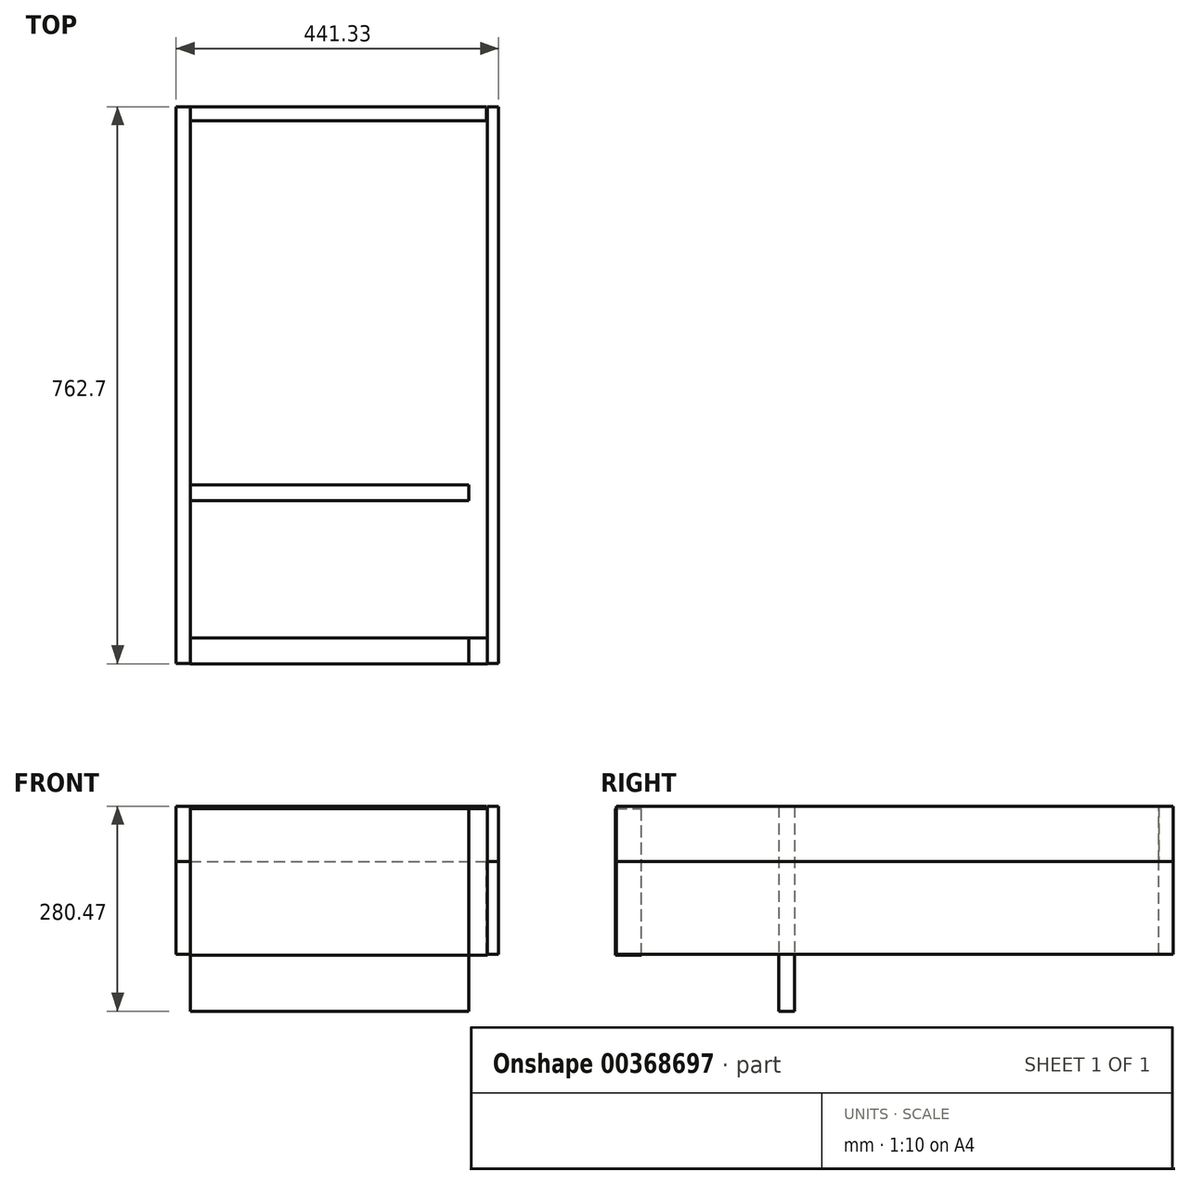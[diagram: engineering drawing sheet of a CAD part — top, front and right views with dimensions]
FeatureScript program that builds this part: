
annotation { "Feature Type Name" : "Feature", "Feature Type Description" : "" }
export const myFeature = defineFeature(function(context is Context, id is Id, definition is map)
    precondition{}
    {
        {
            var Q0;
            Q0=qCreatedBy(makeId("Front.planeOp"),FACE);
            var sketch = newSketch(context, id + "F0", { "sketchPlane" : qUnion([Q0])});
            skLineSegment(sketch, "E0.bottom", {"start": v(-75.87, 75.19) * mm, "end": v(75.87, 75.19) * mm});
            skLineSegment(sketch, "E0.top", {"start": v(-75.87, 0) * mm, "end": v(75.87, 0) * mm});
            skLineSegment(sketch, "E0.left", {"start": v(-75.87, 75.19) * mm, "end": v(-75.87, 0) * mm});
            skLineSegment(sketch, "E0.right", {"start": v(75.87, 75.19) * mm, "end": v(75.87, 0) * mm});
            skSolve(sketch);
        }
        {
            var Q0;
            Q0=makeQuery(id+"F0.imprint","IMPRINT",FACE,{"disambiguationData":[TD([[makeQuery(id+"F0.imprint","IMPRINT",EDGE,{"derivedFrom":sQuery(id+"F0.wireOp",EDGE,"E0.bottom")}),-1.0]])]});
            extrude(context, id + "F1", {"entities" : qUnion([Q0]), "depth" : 19.05 * mm});
        }
        {
            var Q0;
            Q0=qCreatedBy(makeId("Front.planeOp"),FACE);
            var sketch = newSketch(context, id + "F2", { "sketchPlane" : qUnion([Q0])});
            skLineSegment(sketch, "E1.bottom", {"start": v(-75.82, 75.3) * mm, "end": v(-94.93, 75.3) * mm});
            skLineSegment(sketch, "E1.top", {"start": v(-75.82, 3.74) * mm, "end": v(-94.93, 3.74) * mm});
            skLineSegment(sketch, "E1.left", {"start": v(-75.82, 75.3) * mm, "end": v(-75.82, 3.74) * mm});
            skLineSegment(sketch, "E1.right", {"start": v(-94.93, 75.3) * mm, "end": v(-94.93, 3.74) * mm});
            skSolve(sketch);
        }
        {
            var Q0;
            Q0=makeQuery(id+"F2.imprint","IMPRINT",FACE,{"disambiguationData":[TD([[makeQuery(id+"F2.imprint","IMPRINT",EDGE,{"derivedFrom":sQuery(id+"F2.wireOp",EDGE,"E1.bottom")}),1.0]])]});
            extrude(context, id + "F3", {"entities" : qUnion([Q0]), "operationType" : NewBodyOperationType.ADD, "depth" : 762 * mm});
        }
        {
            var Q0;
            Q0=makeQuery(id+"F3.opExtrude","SWEPT_FACE",FACE,{"disambiguationData":[OSD([sQuery(id+"F2.wireOp",EDGE,"E1.top")])]});
            extrude(context, id + "F4", {"entities" : qUnion([Q0]), "operationType" : NewBodyOperationType.ADD, "depth" : 3.8 * mm});
        }
        {
            var Q0;
            Q0=makeQuery(id+"F1.opExtrude","SWEPT_FACE",FACE,{"disambiguationData":[OSD([sQuery(id+"F0.wireOp",EDGE,"E0.right")])]});
            extrude(context, id + "F5", {"entities" : qUnion([Q0]), "operationType" : NewBodyOperationType.ADD, "depth" : 254 * mm});
        }
        {
            var Q0;
            Q0=qCreatedBy(makeId("Front.planeOp"),FACE);
            var sketch = newSketch(context, id + "F6", { "sketchPlane" : qUnion([Q0])});
            skLineSegment(sketch, "E2.bottom", {"start": v(330.75, 0) * mm, "end": v(346.4, 0) * mm});
            skLineSegment(sketch, "E2.top", {"start": v(330.75, 74.95) * mm, "end": v(346.4, 74.95) * mm});
            skLineSegment(sketch, "E2.left", {"start": v(330.75, 0) * mm, "end": v(330.75, 74.95) * mm});
            skLineSegment(sketch, "E2.right", {"start": v(346.4, 0) * mm, "end": v(346.4, 74.95) * mm});
            skSolve(sketch);
        }
        {
            var Q0;
            Q0=makeQuery(id+"F6.imprint","IMPRINT",FACE,{"disambiguationData":[TD([[makeQuery(id+"F6.imprint","IMPRINT",EDGE,{"derivedFrom":sQuery(id+"F6.wireOp",EDGE,"E2.bottom")}),1.0]])]});
            extrude(context, id + "F7", {"entities" : qUnion([Q0]), "depth" : 762 * mm});
        }
        {
            var Q0;
            Q0=makeQuery(id+"F4.opExtrude","CAP_FACE",FACE,{"disambiguationData":[OSD([sQuery(id+"F2.wireOp",EDGE,"E1.top")])],"isStart":false});
            var Q1;
            {var subQ0=sQuery(id+"F0.wireOp",EDGE,"E0.top");Q1=makeQuery(id+"F5.boolean.opBoolean","MERGE",FACE,{"derivedFrom":[makeQuery(id+"F1.opExtrude","SWEPT_FACE",FACE,{"disambiguationData":[OSD([subQ0])]}),makeQuery(id+"F5.opExtrude","SWEPT_FACE",FACE,{"disambiguationData":[OSD([subQ0,sQuery(id+"F0.wireOp",EDGE,"E0.right")])]})]});}
            var Q2;
            Q2=makeQuery(id+"F7.opExtrude","SWEPT_FACE",FACE,{"disambiguationData":[OSD([sQuery(id+"F6.wireOp",EDGE,"E2.bottom")])]});
            extrude(context, id + "F8", {"entities" : qUnion([Q0, Q1, Q2]), "depth" : 127 * mm});
        }
        {
            var Q0;
            Q0=makeQuery(id+"F8.opExtrude","SWEPT_FACE",FACE,{"disambiguationData":[OSD([sQuery(id+"F6.wireOp",EDGE,"E2.bottom"),sQuery(id+"F6.wireOp",EDGE,"E2.left")])]});
            cPlane(context, id + "F9", {"entities" : qUnion([Q0]), "cplaneType" : CPlaneType.OFFSET, "offset" : 25.4 * mm, "width" : 152.4 * mm, "height" : 152.4 * mm});
        }
        {
            var Q0;
            Q0=qCreatedBy(id+"F9.planeOp",FACE);
            var sketch = newSketch(context, id + "F10", { "sketchPlane" : qUnion([Q0])});
            skLineSegment(sketch, "E3.bottom", {"start": v(762.7, -128.5) * mm, "end": v(727.2, -128.5) * mm});
            skLineSegment(sketch, "E3.top", {"start": v(762.7, 72.35) * mm, "end": v(727.2, 72.35) * mm});
            skLineSegment(sketch, "E3.left", {"start": v(762.7, -128.5) * mm, "end": v(762.7, 72.35) * mm});
            skLineSegment(sketch, "E3.right", {"start": v(727.2, -128.5) * mm, "end": v(727.2, 72.35) * mm});
            skSolve(sketch);
        }
        {
            var Q0;
            Q0=makeQuery(id+"F10.imprint","IMPRINT",FACE,{"disambiguationData":[TD([[makeQuery(id+"F10.imprint","IMPRINT",EDGE,{"derivedFrom":sQuery(id+"F10.wireOp",EDGE,"E3.bottom")}),-1.0]])]});
            extrude(context, id + "F11", {"entities" : qUnion([Q0]), "depth" : 381 * mm});
        }
        {
            var Q0;
            Q0=makeQuery(id+"F11.opExtrude","CAP_FACE",FACE,{"disambiguationData":[OSD([sQuery(id+"F10.wireOp",EDGE,"E3.bottom"),sQuery(id+"F10.wireOp",EDGE,"E3.top"),sQuery(id+"F10.wireOp",EDGE,"E3.left"),sQuery(id+"F10.wireOp",EDGE,"E3.right")])],"isStart":true});
            extrude(context, id + "F12", {"entities" : qUnion([Q0]), "depth" : 25.4 * mm});
        }
        {
            var Q0;
            Q0=qCreatedBy(id+"F9.planeOp",FACE);
            var sketch = newSketch(context, id + "F13", { "sketchPlane" : qUnion([Q0])});
            skLineSegment(sketch, "E4.bottom", {"start": v(517.63, 74.75) * mm, "end": v(539.37, 74.75) * mm});
            skLineSegment(sketch, "E4.top", {"start": v(517.63, -205.17) * mm, "end": v(539.37, -205.17) * mm});
            skLineSegment(sketch, "E4.left", {"start": v(517.63, 74.75) * mm, "end": v(517.63, -205.17) * mm});
            skLineSegment(sketch, "E4.right", {"start": v(539.37, 74.75) * mm, "end": v(539.37, -205.17) * mm});
            skSolve(sketch);
        }
        {
            var Q0;
            Q0=makeQuery(id+"F13.imprint","IMPRINT",FACE,{"disambiguationData":[TD([[makeQuery(id+"F13.imprint","IMPRINT",EDGE,{"derivedFrom":sQuery(id+"F13.wireOp",EDGE,"E4.bottom")}),-1.0]])]});
            extrude(context, id + "F14", {"entities" : qUnion([Q0]), "depth" : 381 * mm});
        }
        {
            var Q0;
            Q0=makeQuery(id+"F14.opExtrude","SWEPT_FACE",FACE,{"disambiguationData":[OSD([sQuery(id+"F13.wireOp",EDGE,"E4.top")])]});
            extrude(context, id + "F15", {"entities" : qUnion([Q0]), "operationType" : NewBodyOperationType.ADD, "depth" : -127 * mm});
        }
    });
